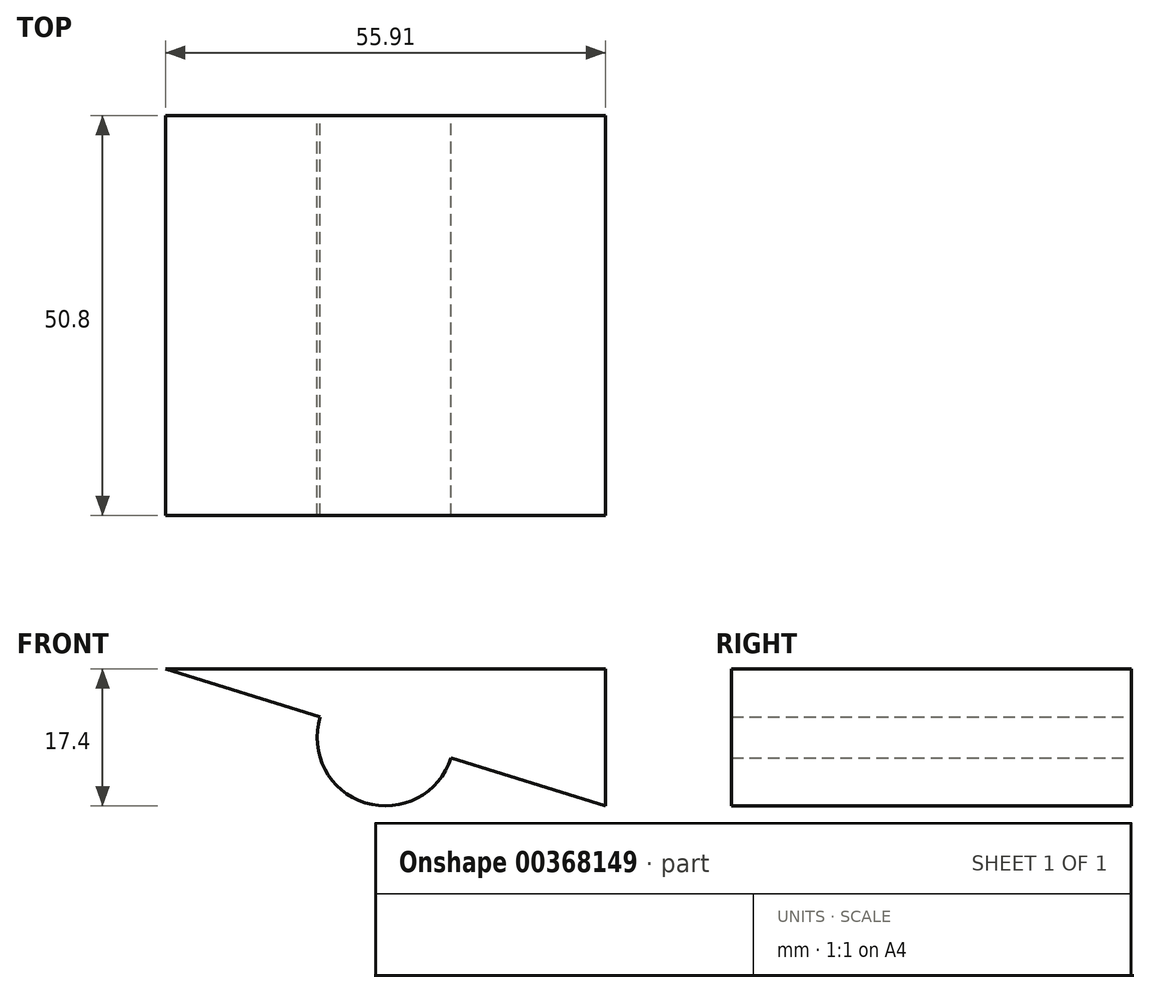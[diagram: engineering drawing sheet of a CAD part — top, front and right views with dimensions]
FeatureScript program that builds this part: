
annotation { "Feature Type Name" : "Feature", "Feature Type Description" : "" }
export const myFeature = defineFeature(function(context is Context, id is Id, definition is map)
    precondition{}
    {
        {
            var Q0;
            Q0=qCreatedBy(makeId("Front.planeOp"),FACE);
            var sketch = newSketch(context, id + "F0", { "sketchPlane" : qUnion([Q0])});
            skLineSegment(sketch, "E0", {"start": v(-31.66, 25.81) * mm, "end": v(24.25, 25.81) * mm});
            skLineSegment(sketch, "E1", {"start": v(24.25, 25.81) * mm, "end": v(24.25, 8.41) * mm});
            skLineSegment(sketch, "E2", {"start": v(24.25, 8.41) * mm, "end": v(4.6, 14.53) * mm});
            skArc(sketch, "E3", {"start": v(-12.01, 19.7) * mm, "mid": v(-6.3, 8.8) * mm, "end": v(4.6, 14.53) * mm});
            skLineSegment(sketch, "E4.trimOffspring", {"start": v(-12.01, 19.7) * mm, "end": v(-31.66, 25.81) * mm});
            skSolve(sketch);
        }
        {
            var Q0;
            Q0=makeQuery(id+"F0.imprint","IMPRINT",FACE,{"disambiguationData":[TD([[makeQuery(id+"F0.imprint","IMPRINT",EDGE,{"derivedFrom":sQuery(id+"F0.wireOp",EDGE,"E0")}),-1.0]])]});
            extrude(context, id + "F1", {"entities" : qUnion([Q0]), "depth" : 50.8 * mm});
        }
    });
